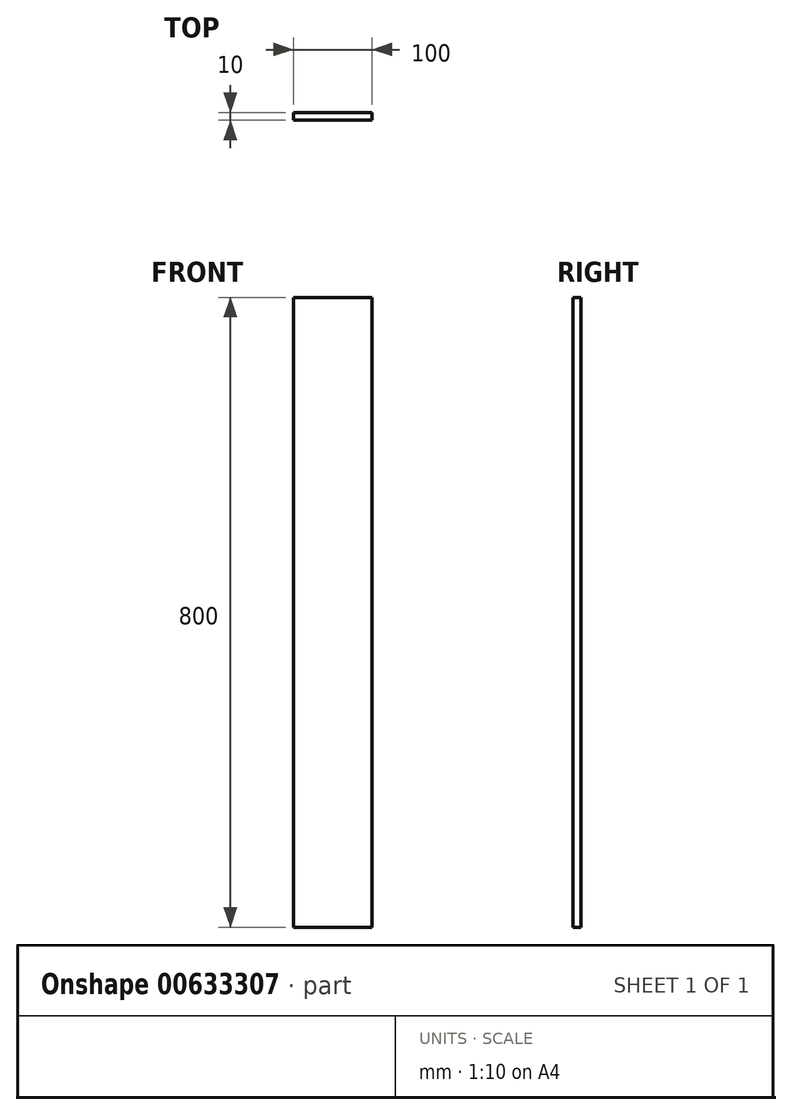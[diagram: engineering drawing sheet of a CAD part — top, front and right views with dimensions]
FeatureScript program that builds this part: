
annotation { "Feature Type Name" : "Feature", "Feature Type Description" : "" }
export const myFeature = defineFeature(function(context is Context, id is Id, definition is map)
    precondition{}
    {
        {
            var Q0;
            Q0=qCreatedBy(makeId("Front.planeOp"),FACE);
            var sketch = newSketch(context, id + "F0", { "sketchPlane" : qUnion([Q0])});
            skLineSegment(sketch, "E0.bottom", {"start": v(50, -400) * mm, "end": v(-50, -400) * mm});
            skLineSegment(sketch, "E0.top", {"start": v(50, 400) * mm, "end": v(-50, 400) * mm});
            skLineSegment(sketch, "E0.left", {"start": v(50, -400) * mm, "end": v(50, 400) * mm});
            skLineSegment(sketch, "E0.right", {"start": v(-50, -400) * mm, "end": v(-50, 400) * mm});
            skPoint(sketch, "E0.middle", {"position": v(0, 0) * mm});
            skSolve(sketch);
        }
        {
            var Q0;
            Q0 = qSketchRegion(id + "F0", true);
            extrude(context, id + "F1", {"entities" : qUnion([Q0]), "endBound" : BoundingType.SYMMETRIC, "depth" : 10 * mm, "offsetDistance" : 25 * mm});
        }
    });
